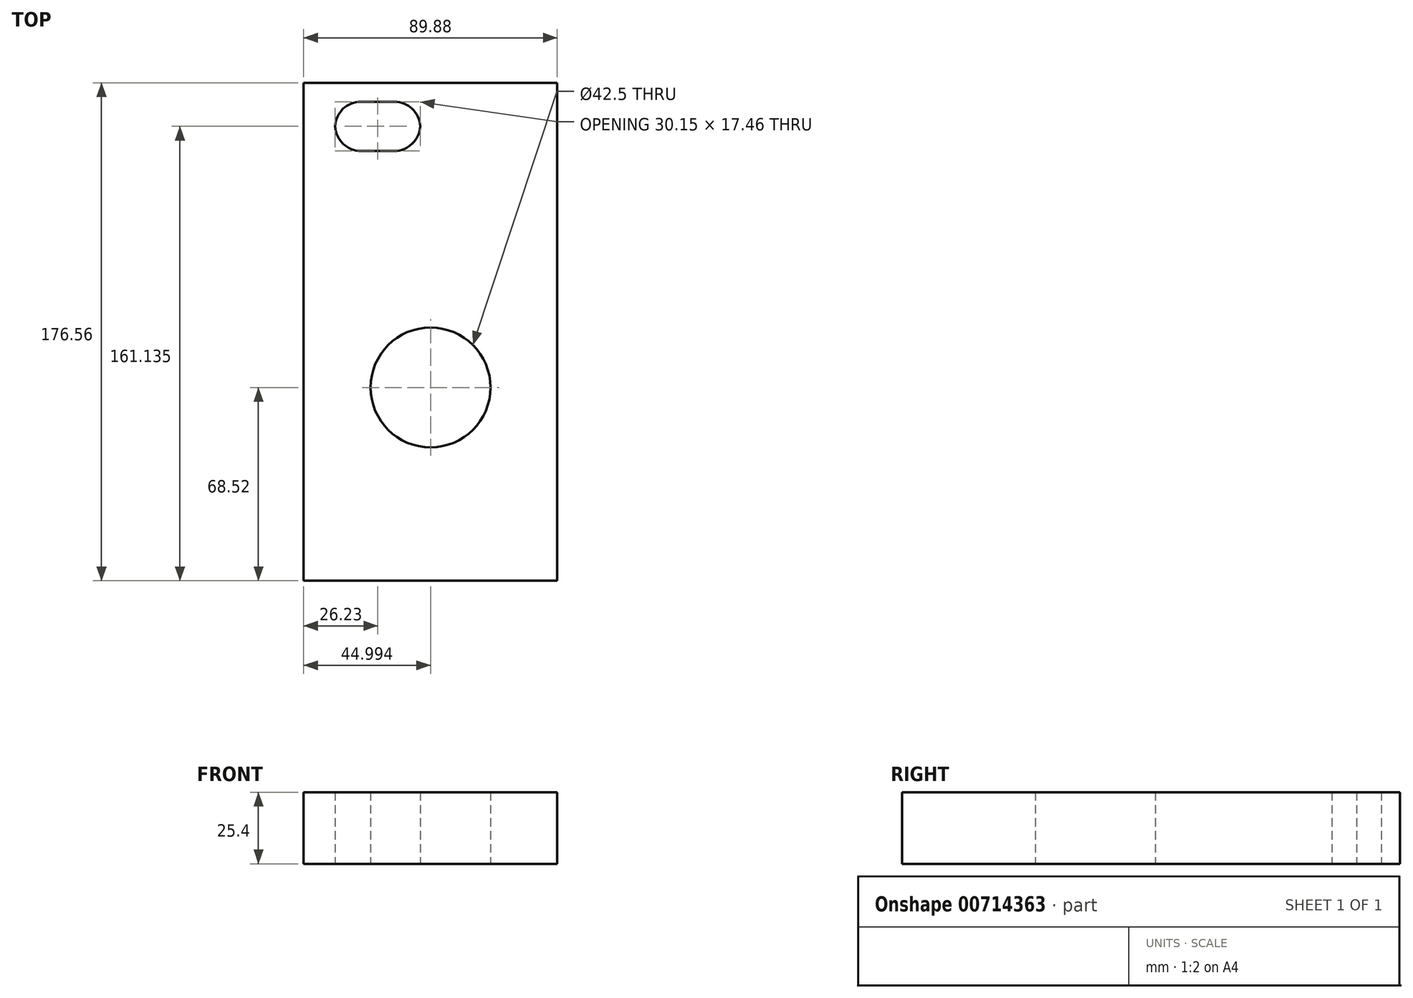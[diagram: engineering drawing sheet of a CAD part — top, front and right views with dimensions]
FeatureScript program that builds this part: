
annotation { "Feature Type Name" : "Feature", "Feature Type Description" : "" }
export const myFeature = defineFeature(function(context is Context, id is Id, definition is map)
    precondition{}
    {
        {
            var Q0;
            Q0=qCreatedBy(makeId("Top.planeOp"),FACE);
            var sketch = newSketch(context, id + "F0", { "sketchPlane" : qUnion([Q0])});
            skLineSegment(sketch, "E0.bottom", {"start": v(-39.66, 127.33) * mm, "end": v(50.22, 127.33) * mm});
            skLineSegment(sketch, "E0.top", {"start": v(-39.66, -49.23) * mm, "end": v(50.22, -49.23) * mm});
            skLineSegment(sketch, "E0.left", {"start": v(-39.66, 127.33) * mm, "end": v(-39.66, -49.23) * mm});
            skLineSegment(sketch, "E0.right", {"start": v(50.22, 127.33) * mm, "end": v(50.22, -49.23) * mm});
            skLineSegment(sketch, "E1", {"start": v(-19.38, 103.17) * mm, "end": v(-7.48, 103.17) * mm});
            skLineSegment(sketch, "E2", {"start": v(-7.48, 120.64) * mm, "end": v(-19.38, 120.64) * mm});
            skArc(sketch, "E3.filletArc", {"start": v(-19.38, 120.64) * mm, "mid": v(-25.84, 117.96) * mm, "end": v(-28.51, 111.5) * mm});
            skArc(sketch, "E4.filletArc", {"start": v(1.65, 111.5) * mm, "mid": v(-1.02, 117.96) * mm, "end": v(-7.48, 120.64) * mm});
            skArc(sketch, "E5.filletArc", {"start": v(-7.48, 103.17) * mm, "mid": v(-1.02, 105.85) * mm, "end": v(1.65, 112.3) * mm});
            skArc(sketch, "E6.filletArc", {"start": v(-28.51, 112.3) * mm, "mid": v(-25.84, 105.85) * mm, "end": v(-19.38, 103.17) * mm});
            skCircle(sketch, "E7", {"center": v(5.33, 19.3) * mm, "radius": 21.25 * mm});
            skSolve(sketch);
        }
        {
            var Q0;
            Q0 = qSketchRegion(id + "F0", true);
            extrude(context, id + "F1", {"entities" : qUnion([Q0]), "depth" : 25.4 * mm, "offsetDistance" : 25.4 * mm});
        }
    });
